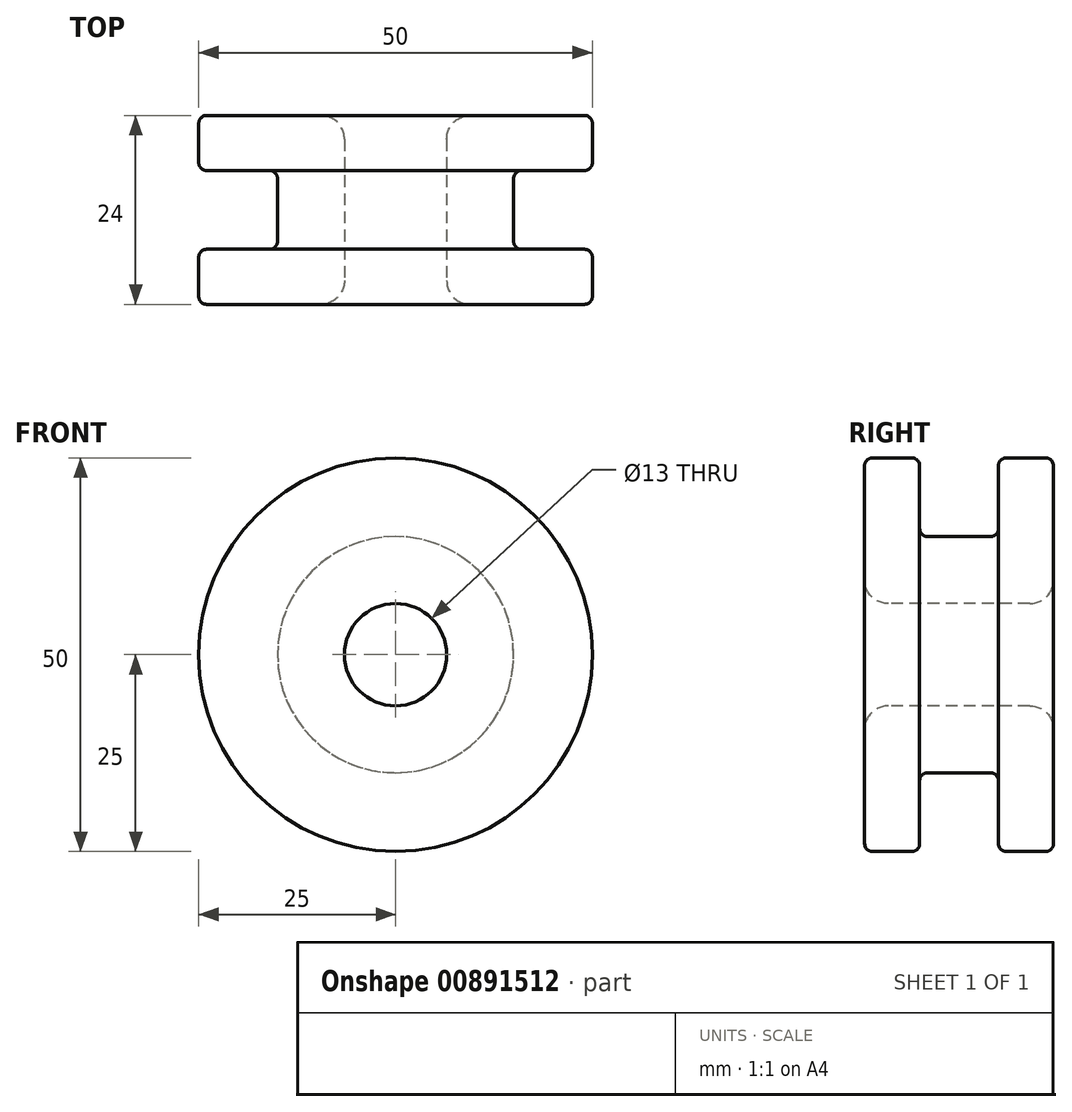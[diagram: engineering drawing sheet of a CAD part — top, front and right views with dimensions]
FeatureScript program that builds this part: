
annotation { "Feature Type Name" : "Feature", "Feature Type Description" : "" }
export const myFeature = defineFeature(function(context is Context, id is Id, definition is map)
    precondition{}
    {
        {
            var Q0;
            Q0=qCreatedBy(makeId("Top.planeOp"),FACE);
            var sketch = newSketch(context, id + "F0", { "sketchPlane" : qUnion([Q0])});
            skLineSegment(sketch, "E0", {"start": v(-6.5, 0) * mm, "end": v(-6.5, 24) * mm});
            skLineSegment(sketch, "E1", {"start": v(-6.5, 24) * mm, "end": v(-25, 24) * mm});
            skLineSegment(sketch, "E2", {"start": v(-25, 24) * mm, "end": v(-25, 17) * mm});
            skLineSegment(sketch, "E3", {"start": v(-25, 17) * mm, "end": v(-15, 17) * mm});
            skLineSegment(sketch, "E4", {"start": v(-15, 17) * mm, "end": v(-15, 7) * mm});
            skLineSegment(sketch, "E5", {"start": v(-15, 7) * mm, "end": v(-25, 7) * mm});
            skLineSegment(sketch, "E6", {"start": v(-25, 7) * mm, "end": v(-25, 0) * mm});
            skLineSegment(sketch, "E7", {"start": v(-25, 0) * mm, "end": v(-6.5, 0) * mm});
            skLineSegment(sketch, "E8", {"start": v(0, 0) * mm, "end": v(0, 24) * mm, "construction": true});
            skSolve(sketch);
        }
        {
            var Q0;
            Q0=makeQuery(id+"F0.imprint","IMPRINT",FACE,{"disambiguationData":[TD([[makeQuery(id+"F0.imprint","IMPRINT",EDGE,{"derivedFrom":sQuery(id+"F0.wireOp",EDGE,"E0")}),1.0]])]});
            var Q1;
            Q1=sQuery(id+"F0.wireOp",EDGE,"E8");
            revolve(context, id + "F1", {"surfaceOperationType" : NewSurfaceOperationType.NEW, "entities" : qUnion([Q0]), "axis" : qUnion([Q1]), "revolveType" : RevolveType.FULL});
        }
        {
            var Q0;
            Q0=makeQuery(id+"F1.opRevolve","SWEPT_EDGE",EDGE,{"disambiguationData":[OSD([sQuery(id+"F0.wireOp",EDGE,"E6"),sQuery(id+"F0.wireOp",EDGE,"E7")])]});
            var Q1;
            Q1=makeQuery(id+"F1.opRevolve","SWEPT_EDGE",EDGE,{"disambiguationData":[OSD([sQuery(id+"F0.wireOp",EDGE,"E5"),sQuery(id+"F0.wireOp",EDGE,"E6")])]});
            var Q2;
            Q2=makeQuery(id+"F1.opRevolve","SWEPT_EDGE",EDGE,{"disambiguationData":[OSD([sQuery(id+"F0.wireOp",EDGE,"E2"),sQuery(id+"F0.wireOp",EDGE,"E3")])]});
            var Q3;
            Q3=makeQuery(id+"F1.opRevolve","SWEPT_EDGE",EDGE,{"disambiguationData":[OSD([sQuery(id+"F0.wireOp",EDGE,"E1"),sQuery(id+"F0.wireOp",EDGE,"E2")])]});
            var Q4;
            Q4=makeQuery(id+"F1.opRevolve","SWEPT_EDGE",EDGE,{"disambiguationData":[OSD([sQuery(id+"F0.wireOp",EDGE,"E4"),sQuery(id+"F0.wireOp",EDGE,"E5")])]});
            var Q5;
            Q5=makeQuery(id+"F1.opRevolve","SWEPT_EDGE",EDGE,{"disambiguationData":[OSD([sQuery(id+"F0.wireOp",EDGE,"E3"),sQuery(id+"F0.wireOp",EDGE,"E4")])]});
            fillet(context, id + "F2", {"entities" : qUnion([Q0, Q1, Q2, Q3, Q4, Q5]), "radius" : 1 * mm, "tangentPropagation" : true, "allowEdgeOverflow" : false});
        }
        {
            var Q0;
            Q0=makeQuery(id+"F1.opRevolve","SWEPT_EDGE",EDGE,{"disambiguationData":[OSD([sQuery(id+"F0.wireOp",EDGE,"E0"),sQuery(id+"F0.wireOp",EDGE,"E1")])]});
            var Q1;
            Q1=makeQuery(id+"F1.opRevolve","SWEPT_EDGE",EDGE,{"disambiguationData":[OSD([sQuery(id+"F0.wireOp",EDGE,"E0"),sQuery(id+"F0.wireOp",EDGE,"E7")])]});
            fillet(context, id + "F3", {"entities" : qUnion([Q0, Q1]), "radius" : 3 * mm, "tangentPropagation" : true, "allowEdgeOverflow" : false});
        }
    });
